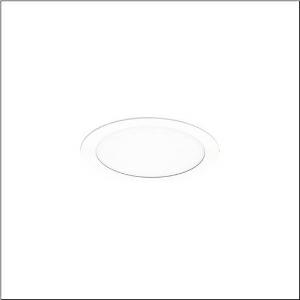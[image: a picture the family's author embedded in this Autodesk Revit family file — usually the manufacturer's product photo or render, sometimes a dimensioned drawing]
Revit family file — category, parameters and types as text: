
# Revit family: lunis_21_l_51db16md91c
name_source: partatom
category: Lighting Fixtures
units: mm (PartAtom-declared; Revit-internal decimal feet)

## family parameters
Cut with Voids When Loaded = No
Host = Face
Light Source = No
Part Type = Normal
Room Calculation Point = No
Round Connector Dimension = Use Diameter
Shared = No

## types (1)
- --- (1 x LED, 3020 lm, 21.7 W, 6500K)
    Apparent Load = 22 VA
    CIE Flux Codes = 50 80 96 100 100
    Color Rendering = 80
    Color Temperature = 6500K
    Default Elevation = 1800 mm
    Description = Lunis 21,  L, downlight, light control with lens, of PMMA, optical cover: cover panel, of PC, opal, light emission: direct distribution, LED rated luminous flux: 1.750lm, light colour: 830/840/865, with terminal, 3-pole, mains connection: 220..240V, AC/DC, 0/50..60Hz, housing, round, of diecast aluminium, traffic white (RAL 9016), diameter: 165mm, clamping range: 1..40mm, protection rating (complete): IP20, protection rating (on room side): IP54, insulation class (complete): insulation class II (safety insulation), certification: CE, impact resistance: IK03, packaging unit: 1 piece
    Height = 0 mm  [stored 0 ft]
    Lamp = 1 x LED
    Lamp Light Flux = 3020 lm
    Lamp Power = 21.7 W
    Lamp count = 1
    Length = 165 mm
    Luminous efficacy = 139 lm/W
    Manufacturer = Siteco
    ModVariant = No
    Model = 51DB16MD91C
    Mounting Place = Ceiling
    Mounting Type = Recessed
    Number of Poles = 1
    OnlyDefault = Yes
    Power Factor = 1
    Product Name = Lunis 21 L
    Product group = downlight
    ProductGroupID = 400
    Protection Class = Protection class II
    Protection Degree = IP 20
    RLX_Detail_Level = 1
    RLX_Emergency_Light_Flux = 0 lm
    RLX_Emergency_Type = 0
    RLX_Emergency_Type_DB = No
    RlxData = <blob elided: 13741 chars, md5=f84f472e>
    Socket = socket
    Standby Power = 0 W
    System Light Flux = 3020 lm
    System Power = 22 W
    Type Comments = individual setting: colour temperature 6500K, luminous flux: 100 % | (OFF | ON | ON | ON) | 650 mA
    Type Image = l_1291165.jpg
    URL = http://relux.com
    VarID = @adj_021012
    Voltage = 0 V
    Weight = 0.00 kg
    Width = 0 mm  [stored 0 ft]

note: [stored X ft] marks values corroborated as IEEE doubles in the binary element streams (Revit-internal decimal feet)

## geometry (parser evidence)
native form markers: Sweep x12
no freeform markers — native parametric forms only
